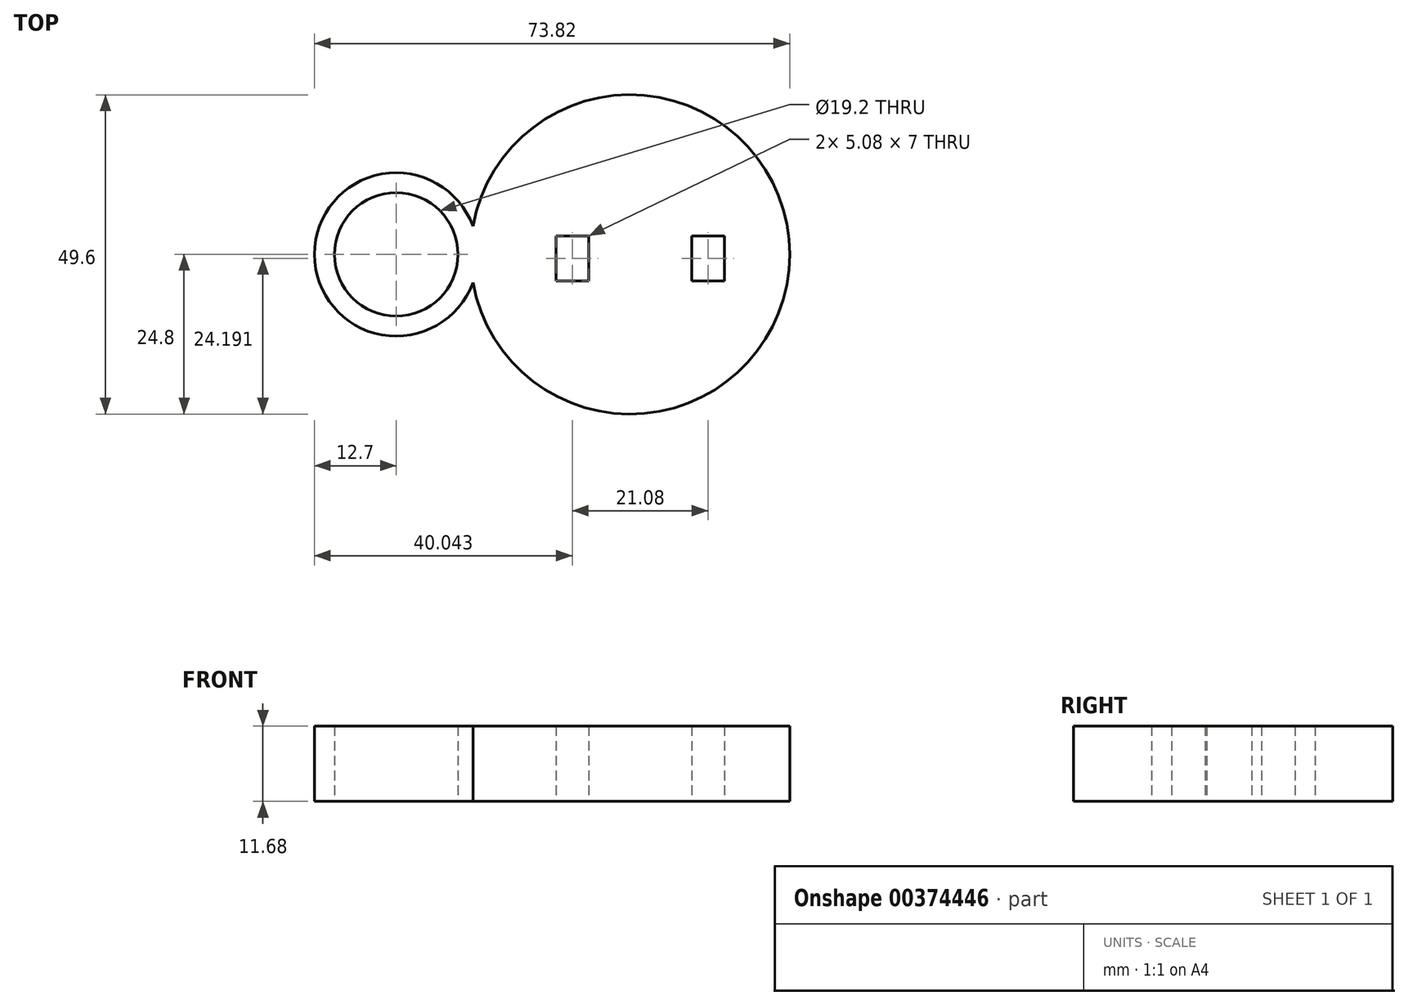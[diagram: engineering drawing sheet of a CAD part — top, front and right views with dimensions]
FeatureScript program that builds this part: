
annotation { "Feature Type Name" : "Feature", "Feature Type Description" : "" }
export const myFeature = defineFeature(function(context is Context, id is Id, definition is map)
    precondition{}
    {
        {
            var Q0;
            Q0=qCreatedBy(makeId("Top.planeOp"),FACE);
            var sketch = newSketch(context, id + "F0", { "sketchPlane" : qUnion([Q0])});
            skArc(sketch, "E0", {"start": v(11.91, 4.4) * mm, "mid": v(-12.7, 0) * mm, "end": v(11.91, -4.4) * mm});
            skCircle(sketch, "E1", {"center": v(0, 0) * mm, "radius": 9.6 * mm});
            skArc(sketch, "E2", {"start": v(11.91, -4.4) * mm, "mid": v(61.12, 0) * mm, "end": v(11.91, 4.4) * mm});
            skSolve(sketch);
        }
        {
            var Q0;
            Q0=makeQuery(id+"F0.imprint","IMPRINT",FACE,{"disambiguationData":[TD([[makeQuery(id+"F0.imprint","IMPRINT",EDGE,{"derivedFrom":sQuery(id+"F0.wireOp",EDGE,"E0")}),1.0]])]});
            extrude(context, id + "F1", {"entities" : qUnion([Q0]), "depth" : 11.68 * mm});
        }
        {
            var Q0;
            Q0=makeQuery(id+"F1.opExtrude","CAP_FACE",FACE,{"disambiguationData":[OSD([sQuery(id+"F0.wireOp",EDGE,"E0"),sQuery(id+"F0.wireOp",EDGE,"E1"),sQuery(id+"F0.wireOp",EDGE,"E2")])],"isStart":true});
            var sketch = newSketch(context, id + "F2", { "sketchPlane" : qUnion([Q0])});
            skLineSegment(sketch, "E3.bottom", {"start": v(24.8, 4.1) * mm, "end": v(29.88, 4.1) * mm});
            skLineSegment(sketch, "E3.top", {"start": v(24.8, -2.9) * mm, "end": v(29.88, -2.9) * mm});
            skLineSegment(sketch, "E3.left", {"start": v(24.8, 4.1) * mm, "end": v(24.8, -2.9) * mm});
            skLineSegment(sketch, "E3.right", {"start": v(29.88, 4.1) * mm, "end": v(29.88, -2.9) * mm});
            skLineSegment(sketch, "E4.bottom", {"start": v(45.88, 4.1) * mm, "end": v(50.96, 4.1) * mm});
            skLineSegment(sketch, "E4.top", {"start": v(45.88, -2.9) * mm, "end": v(50.96, -2.9) * mm});
            skLineSegment(sketch, "E4.left", {"start": v(45.88, 4.1) * mm, "end": v(45.88, -2.9) * mm});
            skLineSegment(sketch, "E4.right", {"start": v(50.96, 4.1) * mm, "end": v(50.96, -2.9) * mm});
            skSolve(sketch);
        }
        {
            var Q0;
            Q0=makeQuery(id+"F2.imprint","IMPRINT",FACE,{"disambiguationData":[TD([[makeQuery(id+"F2.imprint","IMPRINT",EDGE,{"derivedFrom":sQuery(id+"F2.wireOp",EDGE,"E3.bottom")}),-1.0]])]});
            var Q1;
            Q1=makeQuery(id+"F2.imprint","IMPRINT",FACE,{"disambiguationData":[TD([[makeQuery(id+"F2.imprint","IMPRINT",EDGE,{"derivedFrom":sQuery(id+"F2.wireOp",EDGE,"E4.bottom")}),-1.0]])]});
            extrude(context, id + "F3", {"entities" : qUnion([Q0, Q1]), "operationType" : NewBodyOperationType.REMOVE, "oppositeDirection" : true, "depth" : 25.4 * mm});
        }
    });
